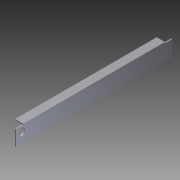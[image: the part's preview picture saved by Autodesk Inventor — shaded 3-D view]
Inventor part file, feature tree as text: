
AUTODESK INVENTOR PART (.ipt)
format: ipt  version: 2012 (Build 160160000, 160)  size: 95,232 bytes
history: native  units: in
note: dims shown in document units (in); Inventor stores cm internally (conversion verified against a paired STEP export)
features: extrude x3, sketch x3
ambient origin geometry x8: Origin, YZ Plane, XZ Plane, XY Plane, X Axis, Y Axis, Z Axis, Center Point
bodies: Solid1 (feature_tree)
feature tree (6):
  extrude  "Extrusion1"  Depth=1.0in
  extrude  "Extrusion2"  Depth=0.125in
  extrude  "Extrusion3"  Depth=0.875in
  sketch  "Sketch1"  dims[d0=2.0in d1=1.0in]
  sketch  "Sketch2"  dims[d2=0.125in d3=0.125in]
  sketch  "Sketch3"  dims[d4=19.0in d5=0.0in d6=0.875in d7=0.75in d8=0.625in d11=20.0in d12=0.0in d13=0.875in d14=0.125in d15=0.0in d16=0.875in]
